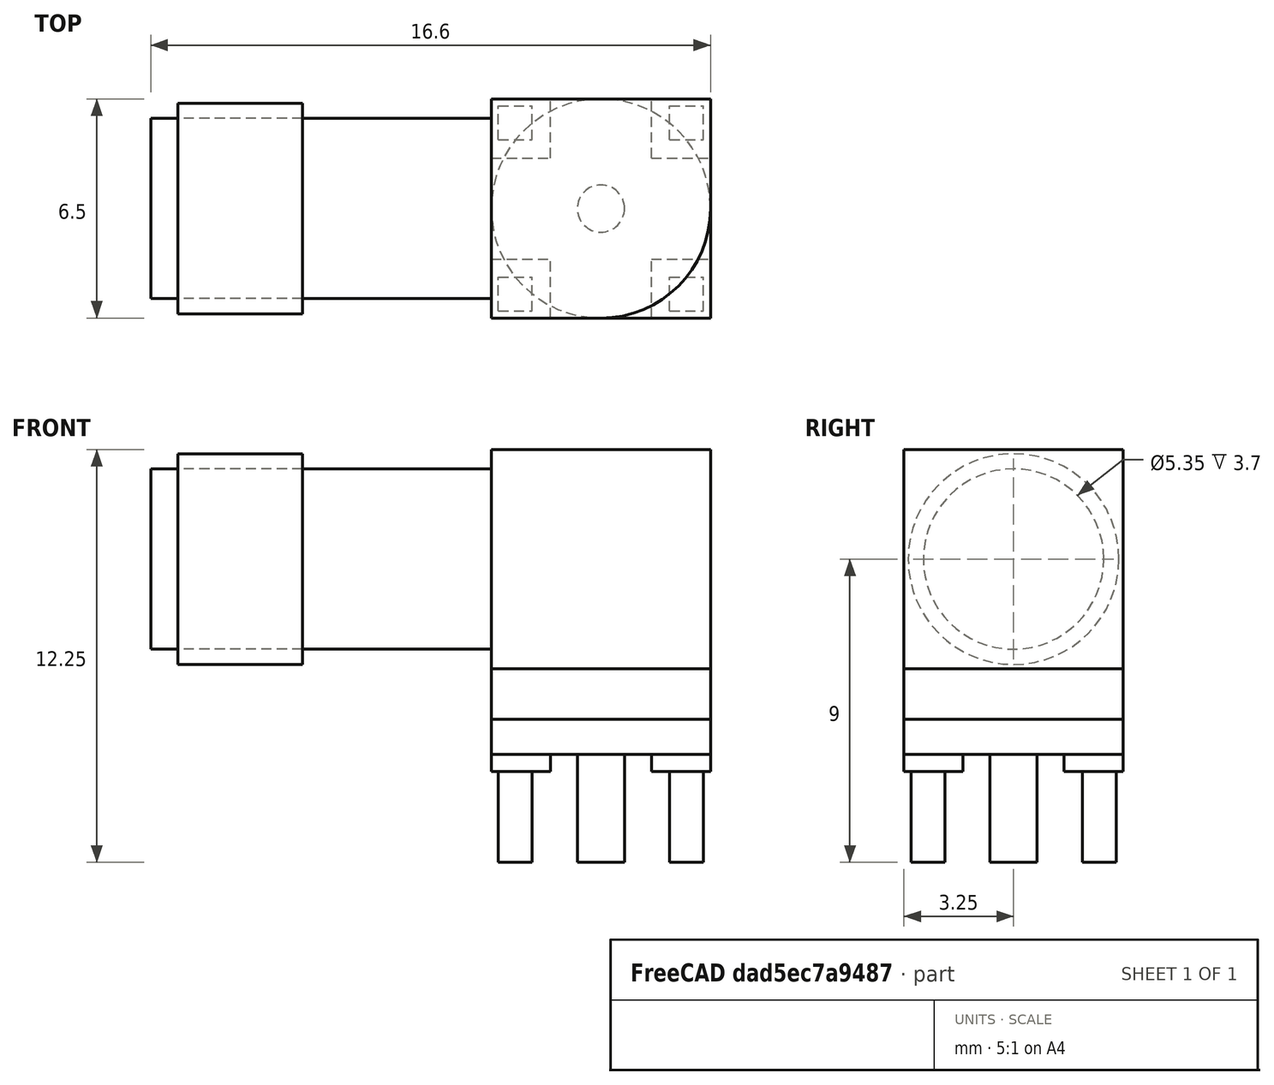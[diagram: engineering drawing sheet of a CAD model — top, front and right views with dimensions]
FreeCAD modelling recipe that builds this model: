
FCSTD DOCUMENT  (FreeCAD 0.19RUnknown)
Label: HJ-SMA003
License: All rights reserved
LicenseURL: http://en.wikipedia.org/wiki/All_rights_reserved
objects: Part::Box×10, Part::Cylinder×3, Part::FeaturePython×1, Part::Compound×1
note: 15 computed .brp shape members not serialized (recipe doc carries the construction recipe); baked Part::Feature solids carry a one-line shape summary decoded from their .brp

FEATURE [Part::Cylinder] Cylinder
  Angle = 360
  AttacherType = Attacher::AttachEngine3D
  Height = 3.2
  Placement = pos=(0,0,-3.2) rot=(0,0,1;0rad)
  Radius = 0.7
FEATURE [Part::Box] Box  label="Cube"
  AttacherType = Attacher::AttachEngine3D
  Height = 1.05
  Length = 6.5
  Placement = pos=(-3.25,-3.25,0) rot=(0,0,1;0rad)
  Width = 6.5
FEATURE [Part::Cylinder] Cylinder001
  Angle = 360
  AttacherType = Attacher::AttachEngine3D
  Height = 1.5
  Placement = pos=(0,0,1.05) rot=(0,0,1;0rad)
  Radius = 3.25
FEATURE [Part::Box] Box001  label="Cube001"
  AttacherType = Attacher::AttachEngine3D
  Height = 6.5
  Length = 6.5
  Placement = pos=(-3.25,-3.25,2.55) rot=(0,0,1;0rad)
  Width = 6.5
FEATURE [Part::Cylinder] Cylinder002
  Angle = 360
  AttacherType = Attacher::AttachEngine3D
  Height = 10.1
  Placement = pos=(-3.25,0,5.8) rot=(0,-1,0;1.5708rad)
  Radius = 2.675
  expr: Radius = 5.35 / 2
FEATURE [Part::FeaturePython] Tube  # WARN: FeaturePython — macro-defined, semantics opaque (R4)
  AttacherType = Attacher::AttachEngine3D
  Height = 3.7
  InnerRadius = 2.675
  OuterRadius = 3.125
  Placement = pos=(-8.85,0,5.8) rot=(0,-1,0;1.5708rad)
  expr: InnerRadius = 5.35 / 2
  expr: OuterRadius = 6.25 / 2
FEATURE [Part::Box] Box002  label="Cube002"
  AttacherType = Attacher::AttachEngine3D
  Height = 0.5
  Length = 1.75
  Placement = pos=(-3.25,-3.25,-0.5) rot=(0,0,1;0rad)
  Width = 1.75
  expr: Length = 3.5 / 2
  expr: Width = 3.5 / 2
FEATURE [Part::Box] Box003  label="Cube003"
  AttacherType = Attacher::AttachEngine3D
  Height = 0.5
  Length = 1.75
  Placement = pos=(-3.25,1.5,-0.5) rot=(0,0,1;0rad)
  Width = 1.75
  expr: Width = 3.5 / 2
  expr: Length = 3.5 / 2
FEATURE [Part::Box] Box004  label="Cube004"
  AttacherType = Attacher::AttachEngine3D
  Height = 0.5
  Length = 1.75
  Placement = pos=(1.5,-3.25,-0.5) rot=(0,0,1;0rad)
  Width = 1.75
  expr: Width = 3.5 / 2
  expr: Length = 3.5 / 2
FEATURE [Part::Box] Box005  label="Cube005"
  AttacherType = Attacher::AttachEngine3D
  Height = 0.5
  Length = 1.75
  Placement = pos=(1.5,1.5,-0.5) rot=(0,0,1;0rad)
  Width = 1.75
  expr: Width = 3.5 / 2
  expr: Length = 3.5 / 2
FEATURE [Part::Box] Box006  label="Cube006"
  AttacherType = Attacher::AttachEngine3D
  Height = 2.7
  Length = 1
  Placement = pos=(-3.04,-3.04,-3.2) rot=(0,0,1;0rad)
  Width = 1
FEATURE [Part::Box] Box007  label="Cube007"
  AttacherType = Attacher::AttachEngine3D
  Height = 2.7
  Length = 1
  Placement = pos=(-3.04,2.04,-3.2) rot=(0,0,1;0rad)
  Width = 1
FEATURE [Part::Box] Box008  label="Cube008"
  AttacherType = Attacher::AttachEngine3D
  Height = 2.7
  Length = 1
  Placement = pos=(2.04,-3.04,-3.2) rot=(0,0,1;0rad)
  Width = 1
FEATURE [Part::Box] Box009  label="Cube009"
  AttacherType = Attacher::AttachEngine3D
  Height = 2.7
  Length = 1
  Placement = pos=(2.04,2.04,-3.2) rot=(0,0,1;0rad)
  Width = 1
FEATURE [Part::Compound] Compound
  Links = -> [Cylinder,Box,Cylinder001,Box001,Cylinder002,Tube,Box002,Box003,Box004,Box005,Box006,Box007,Box008,Box009]
